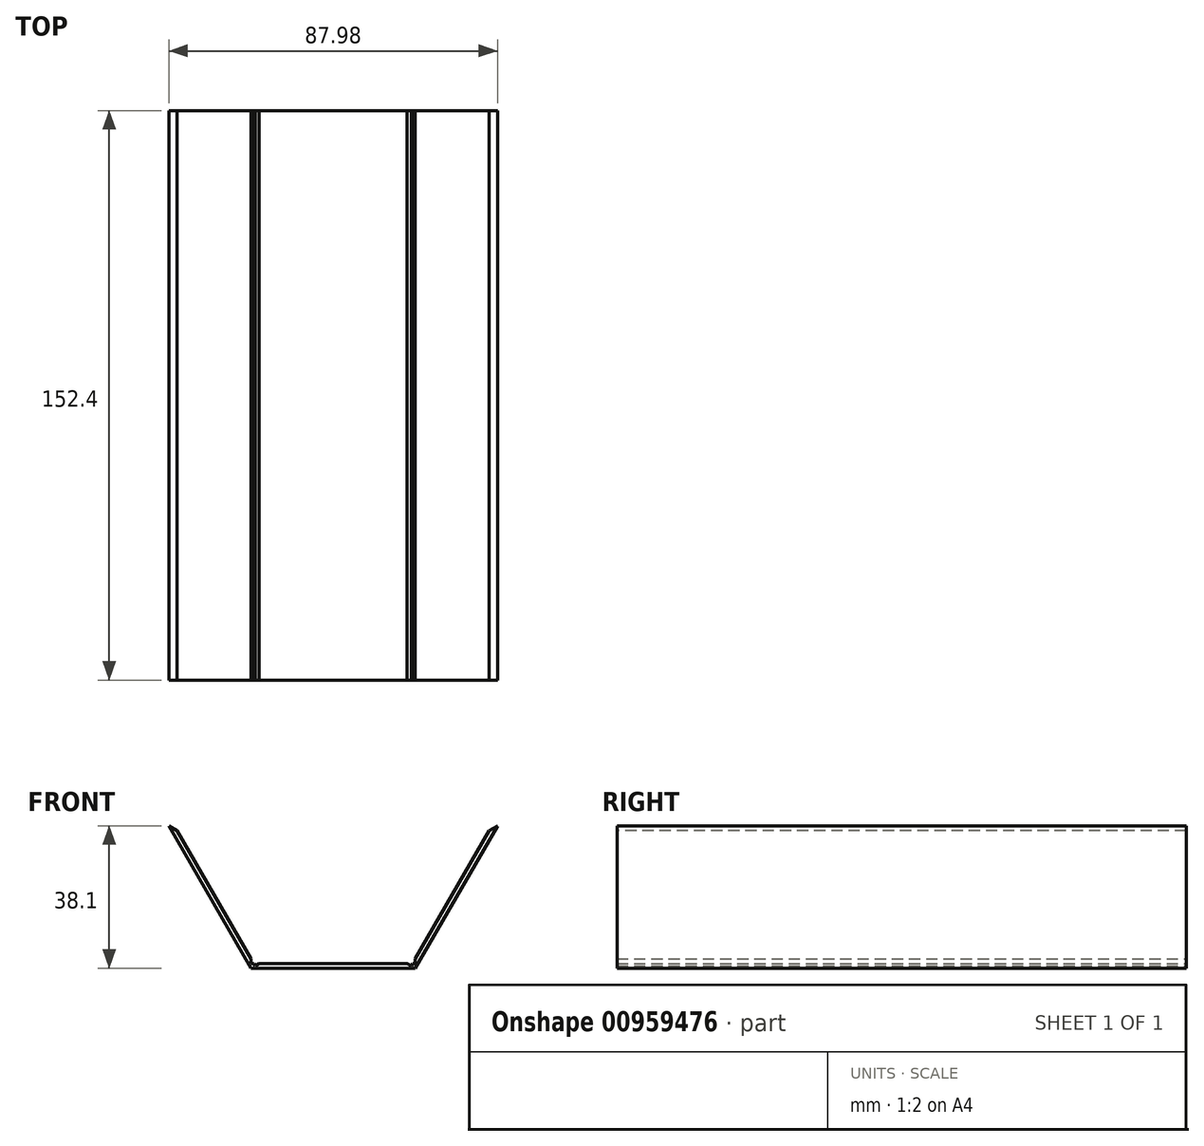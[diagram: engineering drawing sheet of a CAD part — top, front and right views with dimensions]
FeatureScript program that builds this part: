
annotation { "Feature Type Name" : "Feature", "Feature Type Description" : "" }
export const myFeature = defineFeature(function(context is Context, id is Id, definition is map)
    precondition{}
    {
        {
            var Q0;
            Q0=qCreatedBy(makeId("Front.planeOp"),FACE);
            var sketch = newSketch(context, id + "F0", { "sketchPlane" : qUnion([Q0])});
            skCircle(sketch, "E0.cCircle", {"center": v(0, 38.1) * mm, "radius": 38.1 * mm, "construction": true});
            skLineSegment(sketch, "E0.0", {"start": v(22, 76.2) * mm, "end": v(44, 38.1) * mm});
            skLineSegment(sketch, "E0.1", {"start": v(44, 38.1) * mm, "end": v(22, 0) * mm});
            skLineSegment(sketch, "E0.2", {"start": v(22, 0) * mm, "end": v(-22, 0) * mm});
            skLineSegment(sketch, "E0.3", {"start": v(-22, 0) * mm, "end": v(-44, 38.1) * mm});
            skLineSegment(sketch, "E0.4", {"start": v(-44, 38.1) * mm, "end": v(-22, 76.2) * mm});
            skLineSegment(sketch, "E0.5", {"start": v(-22, 76.2) * mm, "end": v(22, 76.2) * mm});
            skPoint(sketch, "E0.0.midPoint", {"position": v(33, 57.15) * mm});
            skSolve(sketch);
        }
        {
            var Q0;
            Q0=makeQuery(id+"F0.imprint","IMPRINT",FACE,{"disambiguationData":[TD([[makeQuery(id+"F0.imprint","IMPRINT",EDGE,{"derivedFrom":sQuery(id+"F0.wireOp",EDGE,"E0.0")}),-1.0]])]});
            extrude(context, id + "F1", {"entities" : qUnion([Q0]), "depth" : 152.4 * mm, "offsetDistance" : 25.4 * mm});
        }
        {
            var Q0;
            Q0=makeQuery(id+"F1.opExtrude","SWEPT_FACE",FACE,{"disambiguationData":[OSD([sQuery(id+"F0.wireOp",EDGE,"E0.0")])]});
            extrude(context, id + "F2", {"entities" : qUnion([Q0]), "operationType" : NewBodyOperationType.REMOVE, "oppositeDirection" : true, "depth" : 74.93 * mm, "offsetDistance" : 25.4 * mm});
        }
        {
            var Q0;
            Q0=makeQuery(id+"F1.opExtrude","SWEPT_FACE",FACE,{"disambiguationData":[OSD([sQuery(id+"F0.wireOp",EDGE,"E0.5")])]});
            extrude(context, id + "F3", {"entities" : qUnion([Q0]), "operationType" : NewBodyOperationType.REMOVE, "oppositeDirection" : true, "depth" : 74.93 * mm, "offsetDistance" : 25.4 * mm});
        }
        {
            var Q0;
            Q0=makeQuery(id+"F1.opExtrude","SWEPT_FACE",FACE,{"disambiguationData":[OSD([sQuery(id+"F0.wireOp",EDGE,"E0.4")])]});
            extrude(context, id + "F4", {"entities" : qUnion([Q0]), "operationType" : NewBodyOperationType.REMOVE, "oppositeDirection" : true, "depth" : 74.93 * mm, "offsetDistance" : 25.4 * mm});
        }
    });
